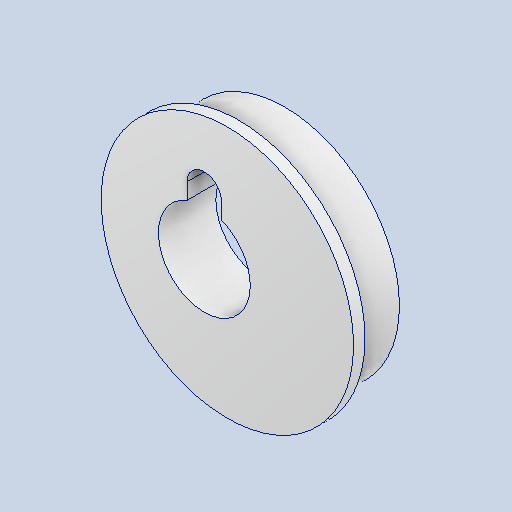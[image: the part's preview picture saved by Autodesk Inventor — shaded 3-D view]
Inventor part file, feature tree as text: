
AUTODESK INVENTOR PART (.ipt)
format: ipt  version: 2024 (Build 280153000, 153)  size: 252,928 bytes
history: native  units: mm
features: sketch x4, extrude x3, other x1, hole x1, projected_geometry x1
ambient origin geometry x8: Origin, YZ Plane, XZ Plane, XY Plane, X Axis, Y Axis, Z Axis, Center Point
bodies: Body1 (feature_tree)
feature tree (10):
  other  "ソリッド1"
  extrude  "押し出し1"  Depth=20.0mm
  extrude  "押し出し2"  Depth=5.0mm TaperAngle=0.0deg
  hole  "穴1"  [1 undecoded]
  extrude  "押し出し3"  Depth=1.0mm TaperAngle=0.0deg
  sketch  "スケッチ1"
  sketch  "スケッチ2"
  projected_geometry  "投影ループ1"
  sketch  "スケッチ3"
  sketch  "スケッチ4"
note: 1 required parameter value undecoded (feature->parameter linkage not recoverable at this tier; creation-order binding heuristic only, values carry confidence <= 0.55)
